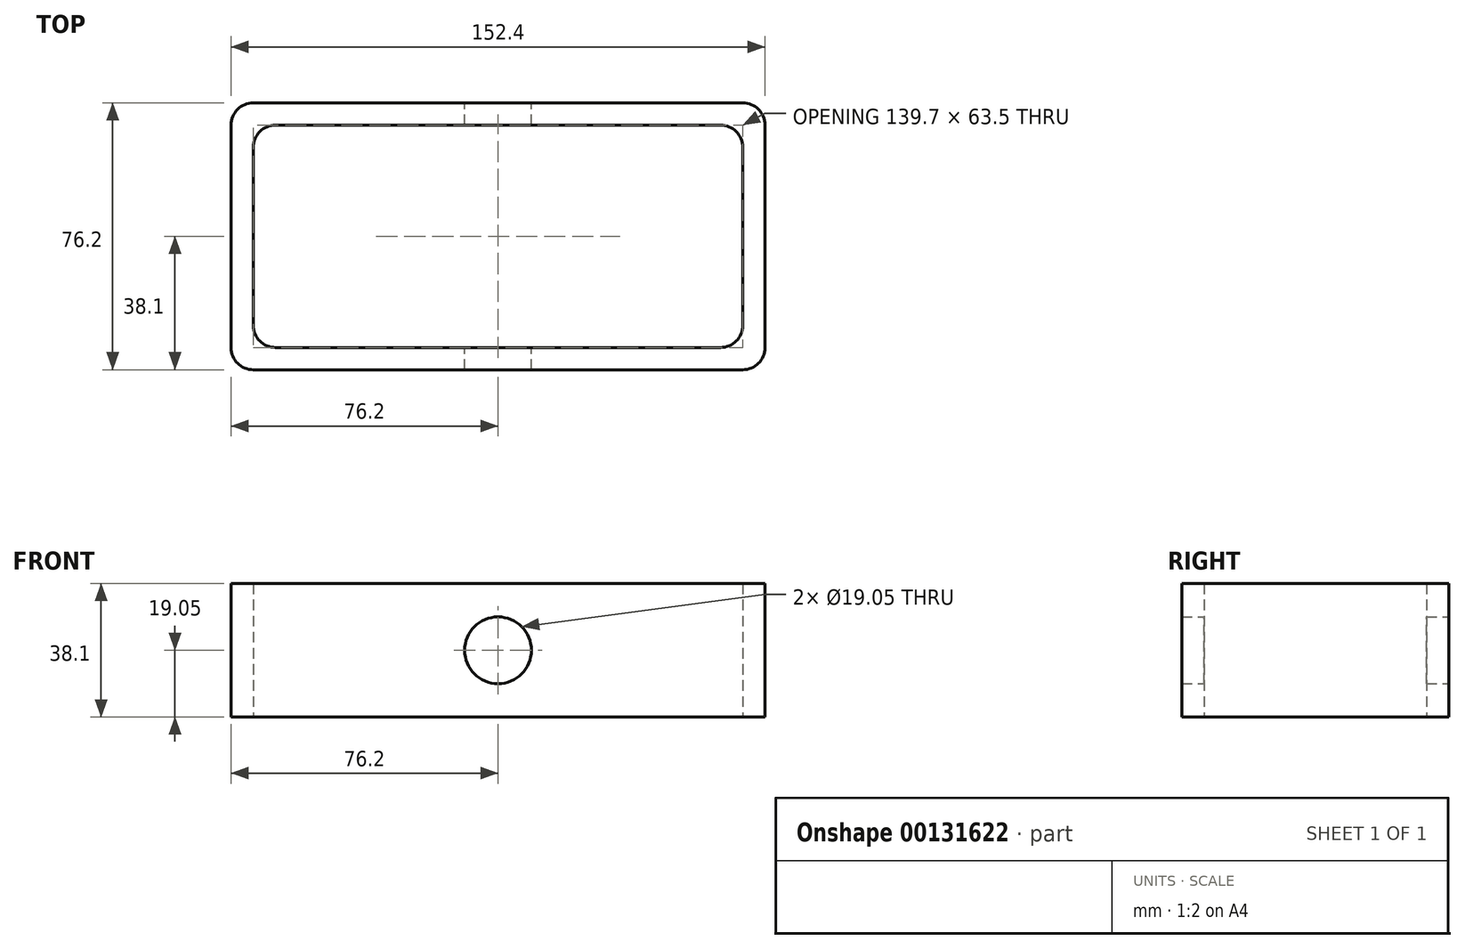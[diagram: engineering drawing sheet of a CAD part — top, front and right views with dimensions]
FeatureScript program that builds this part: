
annotation { "Feature Type Name" : "Feature", "Feature Type Description" : "" }
export const myFeature = defineFeature(function(context is Context, id is Id, definition is map)
    precondition{}
    {
        {
            var Q0;
            Q0=qCreatedBy(makeId("Top.planeOp"),FACE);
            var sketch = newSketch(context, id + "F0", { "sketchPlane" : qUnion([Q0])});
            skLineSegment(sketch, "E0.bottom", {"start": v(76.2, 38.1) * mm, "end": v(-76.2, 38.1) * mm});
            skLineSegment(sketch, "E0.top", {"start": v(76.2, -38.1) * mm, "end": v(-76.2, -38.1) * mm});
            skLineSegment(sketch, "E0.left", {"start": v(76.2, 38.1) * mm, "end": v(76.2, -38.1) * mm});
            skLineSegment(sketch, "E0.right", {"start": v(-76.2, 38.1) * mm, "end": v(-76.2, -38.1) * mm});
            skPoint(sketch, "E0.middle", {"position": v(0, 0) * mm});
            skLineSegment(sketch, "E1.0", {"start": v(69.85, 31.75) * mm, "end": v(-69.85, 31.75) * mm});
            skLineSegment(sketch, "E1.1", {"start": v(69.85, 31.75) * mm, "end": v(69.85, -31.75) * mm});
            skLineSegment(sketch, "E1.2", {"start": v(69.85, -31.75) * mm, "end": v(-69.85, -31.75) * mm});
            skLineSegment(sketch, "E1.3", {"start": v(-69.85, 31.75) * mm, "end": v(-69.85, -31.75) * mm});
            skSolve(sketch);
        }
        {
            var Q0;
            Q0=makeQuery(id+"F0.imprint","IMPRINT",FACE,{"disambiguationData":[TD([[makeQuery(id+"F0.imprint","IMPRINT",EDGE,{"derivedFrom":sQuery(id+"F0.wireOp",EDGE,"E0.bottom")}),1.0]])]});
            extrude(context, id + "F1", {"entities" : qUnion([Q0]), "endBound" : BoundingType.SYMMETRIC, "depth" : 38.1 * mm});
        }
        {
            var Q0;
            Q0=qCreatedBy(makeId("Front.planeOp"),FACE);
            var sketch = newSketch(context, id + "F2", { "sketchPlane" : qUnion([Q0])});
            skCircle(sketch, "E2", {"center": v(0, 0) * mm, "radius": 9.53 * mm});
            skSolve(sketch);
        }
        {
            var Q0;
            Q0=makeQuery(id+"F2.imprint","IMPRINT",FACE,{"disambiguationData":[TD([[makeQuery(id+"F2.imprint","IMPRINT",EDGE,{"derivedFrom":sQuery(id+"F2.wireOp",EDGE,"E2")}),1.0]])]});
            var Q1;
            Q1=makeQuery(id+"F1.opExtrude","SWEPT_FACE",FACE,{"disambiguationData":[OSD([sQuery(id+"F0.wireOp",EDGE,"E0.top")])]});
            var Q2;
            Q2=makeQuery(id+"F1.opExtrude","SWEPT_FACE",FACE,{"disambiguationData":[OSD([sQuery(id+"F0.wireOp",EDGE,"E0.bottom")])]});
            extrude(context, id + "F3", {"entities" : qUnion([Q0]), "operationType" : NewBodyOperationType.REMOVE, "endBound" : BoundingType.UP_TO_SURFACE, "endBoundEntityFace" : qUnion([Q1]), "depth" : 25.4 * mm, "hasSecondDirection" : true, "secondDirectionBound" : SecondDirectionBoundingType.UP_TO_SURFACE, "secondDirectionOppositeDirection" : true, "secondDirectionBoundEntityFace" : qUnion([Q2]), "secondDirectionDepth" : 25.4 * mm});
        }
        {
            var Q0;
            Q0=makeQuery(id+"F1.opExtrude","SWEPT_EDGE",EDGE,{"disambiguationData":[OSD([sQuery(id+"F0.wireOp",EDGE,"E1.2"),sQuery(id+"F0.wireOp",EDGE,"E1.3")])]});
            var Q1;
            Q1=makeQuery(id+"F1.opExtrude","SWEPT_EDGE",EDGE,{"disambiguationData":[OSD([sQuery(id+"F0.wireOp",EDGE,"E1.0"),sQuery(id+"F0.wireOp",EDGE,"E1.3")])]});
            var Q2;
            Q2=makeQuery(id+"F1.opExtrude","SWEPT_EDGE",EDGE,{"disambiguationData":[OSD([sQuery(id+"F0.wireOp",EDGE,"E1.0"),sQuery(id+"F0.wireOp",EDGE,"E1.1")])]});
            var Q3;
            Q3=makeQuery(id+"F1.opExtrude","SWEPT_EDGE",EDGE,{"disambiguationData":[OSD([sQuery(id+"F0.wireOp",EDGE,"E1.1"),sQuery(id+"F0.wireOp",EDGE,"E1.2")])]});
            var Q4;
            Q4=makeQuery(id+"F1.opExtrude","SWEPT_EDGE",EDGE,{"disambiguationData":[OSD([sQuery(id+"F0.wireOp",EDGE,"E0.top"),sQuery(id+"F0.wireOp",EDGE,"E0.right")])]});
            var Q5;
            Q5=makeQuery(id+"F1.opExtrude","SWEPT_EDGE",EDGE,{"disambiguationData":[OSD([sQuery(id+"F0.wireOp",EDGE,"E0.top"),sQuery(id+"F0.wireOp",EDGE,"E0.left")])]});
            var Q6;
            Q6=makeQuery(id+"F1.opExtrude","SWEPT_EDGE",EDGE,{"disambiguationData":[OSD([sQuery(id+"F0.wireOp",EDGE,"E0.bottom"),sQuery(id+"F0.wireOp",EDGE,"E0.left")])]});
            var Q7;
            Q7=makeQuery(id+"F1.opExtrude","SWEPT_EDGE",EDGE,{"disambiguationData":[OSD([sQuery(id+"F0.wireOp",EDGE,"E0.bottom"),sQuery(id+"F0.wireOp",EDGE,"E0.right")])]});
            fillet(context, id + "F4", {"entities" : qUnion([Q0, Q1, Q2, Q3, Q4, Q5, Q6, Q7]), "radius" : 6.35 * mm, "tangentPropagation" : true, "allowEdgeOverflow" : false});
        }
    });
